# Revit family: URA_Eclairage_de_Securite_URAJET
name_source: partatom
category: Luminaires
units: mm (PartAtom-declared; Revit-internal decimal feet)

## family parameters
Cote de connecteur circulaire = Utiliser le diamètre
Couper avec des vides une fois chargée = Non
Hôte = Face
Partagée = Non
Point de calcul de pièce = Non
Source d'éclairage = Oui
Type d'élément = Normal

## types (17) — shared parameters
ALIMENTATION = central (batterie centrale)
Angle de l'inclinaison = 60.00°
CLASSE_DE_PROTECTION = II
Condition Générale d'Utilisation = https://export.legrand.com
Elévation par défaut = 1219 mm
FORMAT_PRODUIT = rectangle
Fichier de distribution photométrique = generic
Filtre de couleur = 16777215
Gradation des changements de température de couleur de lampe = <Aucun>
MATERIAU_DU_BOITIER = plastique
SOURCE_LUMINEUSE = LED non interchangeable
TYPE_DE_COMMUTATION = circuit permanent/circuit de secours

## per-type parameters (varying)
| type | ADAPTE_AU_TYPE_DE_MARQUAGE | CATEGORIE_PRODUIT | CLASSE_DE_PROTECTION_(IP) | COULEUR_DU_BOITIER | DISTANCE_DE_RECONNAISSANCE | DUREE_DE_GARANTIE_BAES_COMPLET | ETAT_DES_ACCUS | FLUX_LUMINEUX_EN_MODE_D'URGENCE | FONCTION | HAUTEUR/PROFONDEUR | INSTALLATION_DE_SURVEILLANCE | LARGEUR | LONGUEUR | MATERIAU_DU_COUVERCLE | PUISSANCE_DE_LA_LAMPE | REFERENCE_ARTICLE | REF_BATTERIE_DE_RECHANGE | RESERVE_DE_MARCHE | TENSION_NOMINALE_(MAX) | TENSION_NOMINALE_(MIN) | TYPE_DE_MONTAGE | TYPE_DE_TENSION |
| BAES URAONE Etanche évacuation SATI | autocollant | Autonome | IP55 | blanc |  | 2 | NiCd | 45 | Evac | 59.7 | auto-test automatique | 120 | 280 | verre transparent | 4.5 | 111317 | 111906 | 1 | 253 | 207 | pose murale en saillie | CA |
| BAES URAONE Etanche ambiance SATI | autocollant | Autonome | IP55 | blanc |  | 2 | NiCd | 320 | Amb | 59.7 | auto-test automatique | 120 | 280 | verre transparent | 32 | 111327 | 111907 | 1 | 253 | 207 | pose murale en saillie | CA |
| BAES URAONE Etanche bi-fonctions SATI | autocollant | Autonome | IP55 | blanc |  | 2 | NiCd | 45 | BAES+BAEH | 59.7 | auto-test automatique | 120 | 280 | verre transparent | 4.5 | 111347 | 2*111906 | 1 | 253 | 207 | pose murale en saillie | CA |
| BAES URAONE Etanche habitation SATI | autocollant | Autonome | IP55 | blanc |  | 2 | NiCd | 8 | BAEH | 59.7 | auto-test automatique | 120 | 280 | verre transparent | 0.8 | 111337 | 111906 | 1 | 253 | 207 | pose murale en saillie | CA |
| BAES URAONE Etanche évacuation AUTODIAG | autocollant | Autonome | IP55 | blanc |  | 2 | NiCd | 45 | Evac | 59.7 | auto-test automatique | 120 | 280 | verre transparent | 4.5 | 111318 | 111906 | 1 | 253 | 207 | pose murale en saillie | CA |
| BAES URAONE Etanche ambiance AUTODIAG | autocollant | Autonome | IP55 | blanc |  | 2 | NiCd | 320 | Amb | 59.7 | auto-test automatique | 120 | 280 | verre transparent | 32 | 111328 | 111907 | 1 | 253 | 207 | pose murale en saillie | CA |
| BAES URAONE Etanche évacuation ADR | autocollant | Autonome | IP55 | blanc |  | 2 | NiCd | 45 | Evac | 59.7 | auto-test automatique | 120 | 280 | verre transparent | 4.5 | 112319 | 111906 | 1 | 253 | 207 | pose murale en saillie | CA |
| BAES URAONE Etanche ambiance ADR | autocollant | Autonome | IP55 | blanc |  | 2 | NiCd | 320 | Amb | 59.7 | auto-test automatique | 120 | 280 | verre transparent | 32 | 112329 | 111907 | 1 | 253 | 207 | pose murale en saillie | CA |
| BAES URAONE Etanche bi-fonctions ADR | autocollant | Autonome | IP55 | blanc |  | 2 | NiCd | 45 | BAES+BAEH | 59.7 | auto-test automatique | 120 | 280 | verre transparent | 4.5 | 112349 | 2*111906 | 1 | 253 | 207 | pose murale en saillie | CA |
| BAES URAONE Etanche habitation ADR | autocollant | Autonome | IP55 | blanc |  | 2 | NiCd | 8 | BAEH | 59.7 | auto-test automatique | 120 | 280 | verre transparent | 0.8 | 112339 | 111906 | 1 | 253 | 207 | pose murale en saillie | CA |
| LSC URAONE Etanche Evacuation 24/48 | autocollant | LSC | IP55 | gris |  | 2 | non applicable | 45 | Evac | 59.7 | sans | 120 | 280 | verre transparent | 4.5 | 122315 |  | 1 | 48 | 24 | pose murale en saillie | CC |
| LSC URAPROOF Evacuation 110/230 IP 55 | autocollant | LSC | IP55 | blanc | 15 | 4 | non applicable | 45 | Evac | 57 | auto-test automatique | 164.5 | 261.2 | plastique transparent | 0.8 | 127314 |  |  | 230 | 110 | pose murale en saillie | CA/CC |
| LSC URAONE Etanche Evacuation 110/230 | autocollant | LSC | IP42 | gris |  | 2 | non applicable | 45 | Evac | 41 | sans | 110 | 210 | verre transparent | 4.5 | 122314 |  | 1 | 253 | 207 | montage en saillie/encastrement | CA |
| LSC URAPROOF Ambiance 24/48 IP 66 |  | LSC | IP66 | blanc | 15 | 4 | non applicable | 400 | Amb | 57 | auto-test automatique | 164.5 | 261.2 | plastique transparent | 6.6 | 127225 |  |  | 48 | 24 | pose murale en saillie | CC |
| LSC URAPROOF Ambiance 110/230 IP 66 |  | LSC | IP66 | blanc | 15 | 4 | non applicable | 400 | Amb | 57 | auto-test automatique | 164.5 | 261.2 | plastique transparent | 6.6 | 127224 |  |  | 230 | 110 | pose murale en saillie | CA/CC |
| LSC URAONE Etanche Ambiance 24/48 |  | LSC | IP55 | gris |  | 2 | non applicable | 320 | Amb | 59.7 | sans | 120 | 280 | verre transparent | 32 | 122325 |  | 1 | 48 | 24 | pose murale en saillie | CC |
| LSC URAONE Etanche Ambiance 110/230 |  | LSC | IP55 | gris |  | 2 | non applicable | 320 | Amb | 59.7 | sans | 120 | 280 | verre transparent | 32 | 122324 |  | 1 | 253 | 207 | pose murale en saillie | CA |

note: column(s) folded — value = type name in every type: DESIGNATION_ARTICLE
